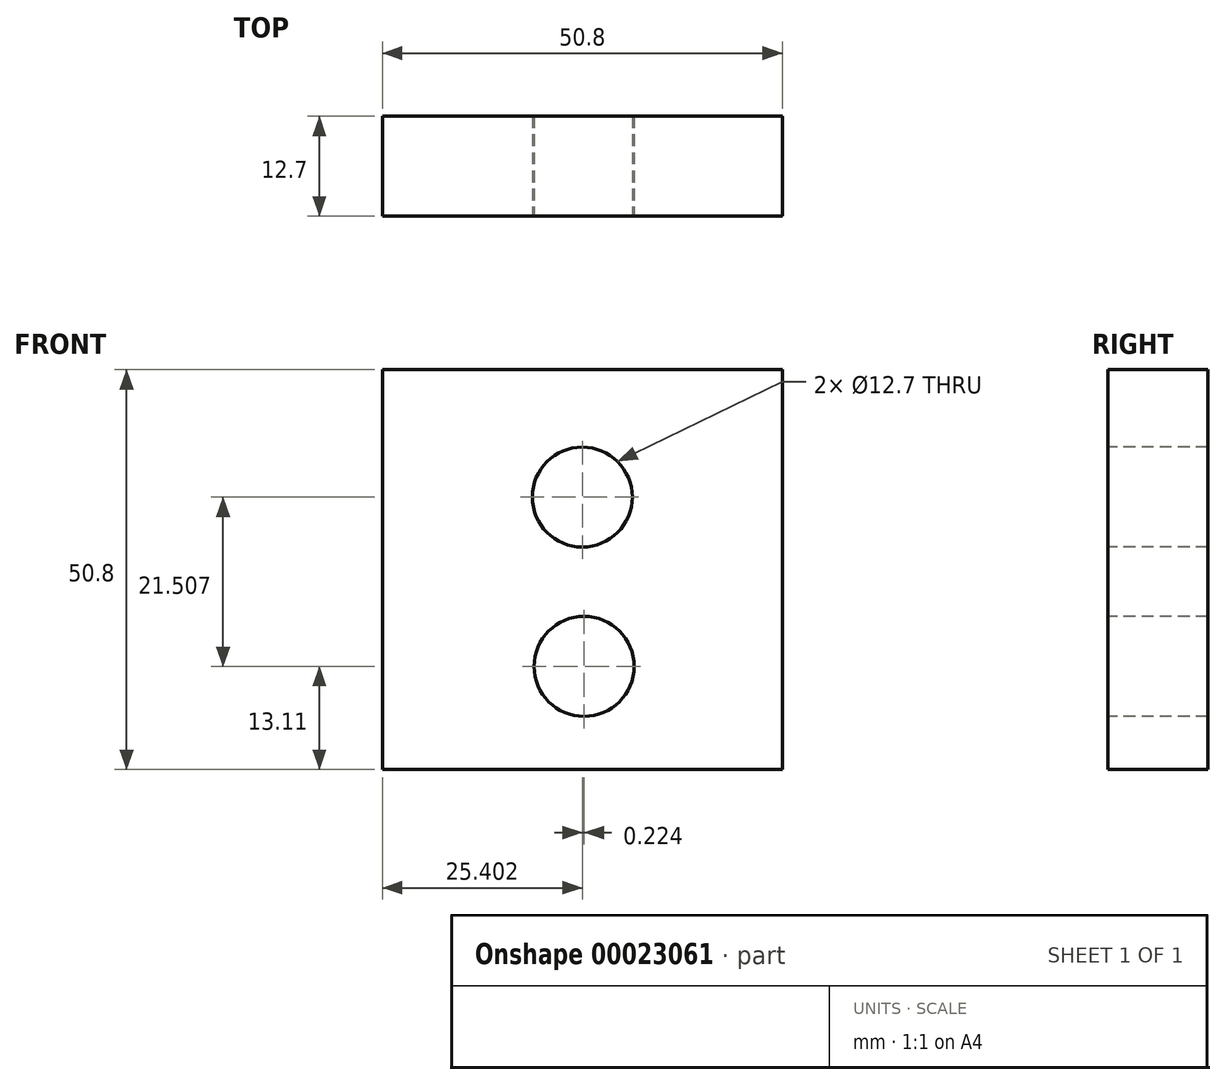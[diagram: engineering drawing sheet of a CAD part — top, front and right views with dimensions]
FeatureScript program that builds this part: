
annotation { "Feature Type Name" : "Feature", "Feature Type Description" : "" }
export const myFeature = defineFeature(function(context is Context, id is Id, definition is map)
    precondition{}
    {
        {
            var Q0;
            Q0=qCreatedBy(makeId("Front.planeOp"),FACE);
            var sketch = newSketch(context, id + "F0", { "sketchPlane" : qUnion([Q0])});
            skLineSegment(sketch, "E0.bottom", {"start": v(0, 0) * mm, "end": v(50.8, 0) * mm});
            skLineSegment(sketch, "E0.top", {"start": v(0, 50.8) * mm, "end": v(50.8, 50.8) * mm});
            skLineSegment(sketch, "E0.left", {"start": v(0, 0) * mm, "end": v(0, 50.8) * mm});
            skLineSegment(sketch, "E0.right", {"start": v(50.8, 0) * mm, "end": v(50.8, 50.8) * mm});
            skPoint(sketch, "E1.orphan", {"position": v(25.4, 50.8) * mm});
            skPoint(sketch, "E2.end.orphan", {"position": v(25.4, 0) * mm});
            skPoint(sketch, "E3", {"position": v(25.18, 13.7) * mm});
            skSolve(sketch);
        }
        {
            var Q0;
            Q0=makeQuery(id+"F0.imprint","IMPRINT",FACE,{"disambiguationData":[TD([[makeQuery(id+"F0.imprint","IMPRINT",EDGE,{"derivedFrom":sQuery(id+"F0.wireOp",EDGE,"E0.bottom")}),1.0]])]});
            var Q1;
            {var subQ3=sQuery(id+"F0.wireOp",EDGE,"E0.top");var subQ5=sQuery(id+"F0.wireOp",EDGE,"E0.left");var subQ7=makeQuery(id+"F0.imprint","INTERSECT",VERTEX,{"derivedFrom":[subQ3,subQ5]});Q1=makeQuery(id+"F0.imprint","IMPRINT",FACE,{"disambiguationData":[TD([[makeQuery(id+"F0.imprint","IMPRINT",EDGE,{"disambiguationData":[TD([[subQ7,-1.0]])],"derivedFrom":subQ3}),-1.0]])]});}
            var Q2;
            {var subQ3=sQuery(id+"F0.wireOp",EDGE,"E0.top");var subQ5=sQuery(id+"F0.wireOp",EDGE,"E0.right");var subQ7=makeQuery(id+"F0.imprint","INTERSECT",VERTEX,{"derivedFrom":[subQ3,subQ5]});Q2=makeQuery(id+"F0.imprint","IMPRINT",FACE,{"disambiguationData":[TD([[makeQuery(id+"F0.imprint","IMPRINT",EDGE,{"disambiguationData":[TD([[subQ7,1.0]])],"derivedFrom":subQ3}),-1.0]])]});}
            extrude(context, id + "F1", {"entities" : qUnion([Q0, Q1, Q2]), "depth" : 12.7 * mm});
        }
        {
            var Q0;
            Q0=makeQuery(id+"F1.opExtrude","CAP_FACE",FACE,{"disambiguationData":[OSD([sQuery(id+"F0.wireOp",EDGE,"E0.bottom"),sQuery(id+"F0.wireOp",EDGE,"E0.top"),sQuery(id+"F0.wireOp",EDGE,"E0.left"),sQuery(id+"F0.wireOp",EDGE,"E0.right")])],"isStart":false});
            var sketch = newSketch(context, id + "F2", { "sketchPlane" : qUnion([Q0])});
            skPoint(sketch, "E4", {"position": v(25.63, 13.11) * mm});
            skSolve(sketch);
        }
        {
            var Q0;
            Q0=sQuery(id+"F2.wireOp",VERTEX,"E4");
            var Q1;
            Q1=makeQuery(id+"F1.opExtrude","SWEPT_BODY",BODY,{"disambiguationData":[OSD([sQuery(id+"F0.wireOp",EDGE,"E0.bottom"),sQuery(id+"F0.wireOp",EDGE,"E0.top"),sQuery(id+"F0.wireOp",EDGE,"E0.left"),sQuery(id+"F0.wireOp",EDGE,"E0.right")])]});
            hole(context, id + "F3", {"style" : HoleStyle.SIMPLE, "holeDiameter" : 12.7 * mm, "endStyle" : HoleEndStyle.THROUGH, "locations" : qUnion([Q0]), "scope" : qUnion([Q1])});
        }
        {
            var Q0;
            Q0=makeQuery(id+"F2.imprint","IMPRINT",FACE,{"disambiguationData":[TD([[makeQuery(id+"F2.imprint","IMPRINT",EDGE,{"derivedFrom":makeQuery(id+"F1.opExtrude","CAP_EDGE",EDGE,{"disambiguationData":[OSD([sQuery(id+"F0.wireOp",EDGE,"E0.bottom")])],"isStart":false})}),1.0]])]});
            var sketch = newSketch(context, id + "F4", { "sketchPlane" : qUnion([Q0])});
            skPoint(sketch, "E5", {"position": v(25.4, 34.62) * mm});
            skSolve(sketch);
        }
        {
            var Q0;
            Q0=sQuery(id+"F4.wireOp",VERTEX,"E5");
            var Q1;
            Q1=makeQuery(id+"F1.opExtrude","SWEPT_BODY",BODY,{"disambiguationData":[OSD([sQuery(id+"F0.wireOp",EDGE,"E0.bottom"),sQuery(id+"F0.wireOp",EDGE,"E0.top"),sQuery(id+"F0.wireOp",EDGE,"E0.left"),sQuery(id+"F0.wireOp",EDGE,"E0.right")])]});
            hole(context, id + "F5", {"style" : HoleStyle.SIMPLE, "holeDiameter" : 12.7 * mm, "endStyle" : HoleEndStyle.THROUGH, "locations" : qUnion([Q0]), "scope" : qUnion([Q1])});
        }
    });
